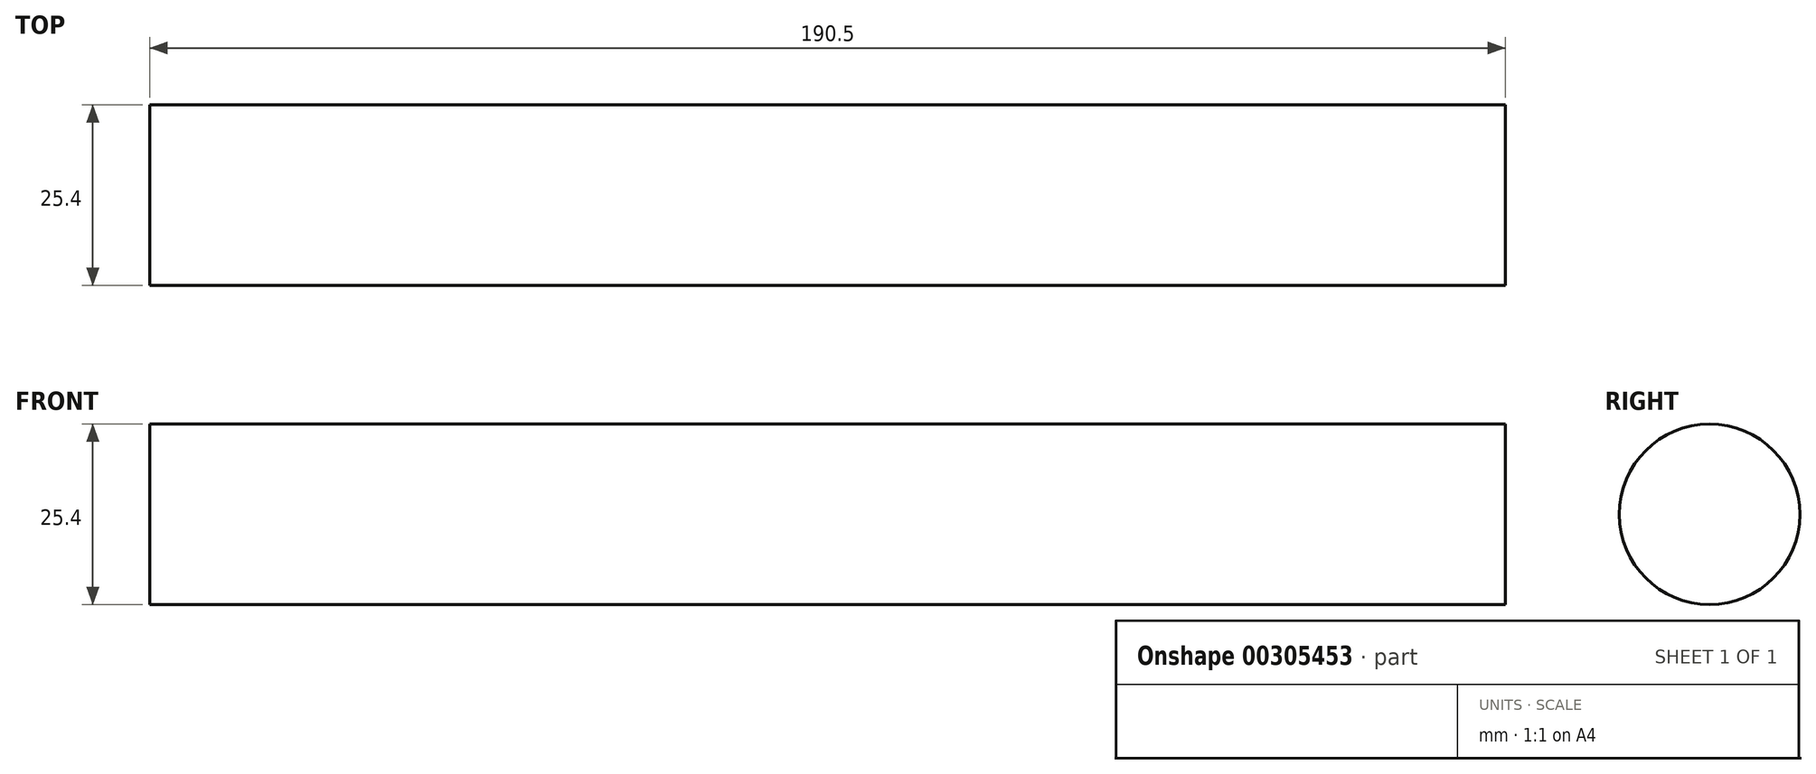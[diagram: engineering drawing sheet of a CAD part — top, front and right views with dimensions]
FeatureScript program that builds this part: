
annotation { "Feature Type Name" : "Feature", "Feature Type Description" : "" }
export const myFeature = defineFeature(function(context is Context, id is Id, definition is map)
    precondition{}
    {
        {
            var Q0;
            Q0=qCreatedBy(makeId("Right.planeOp"),FACE);
            var sketch = newSketch(context, id + "F0", { "sketchPlane" : qUnion([Q0])});
            skCircle(sketch, "E0", {"center": v(-1.51, 0) * mm, "radius": 12.7 * mm});
            skSolve(sketch);
        }
        {
            var Q0;
            Q0 = qSketchRegion(id + "F0", true);
            extrude(context, id + "F1", {"entities" : qUnion([Q0]), "depth" : 190.5 * mm});
        }
    });
